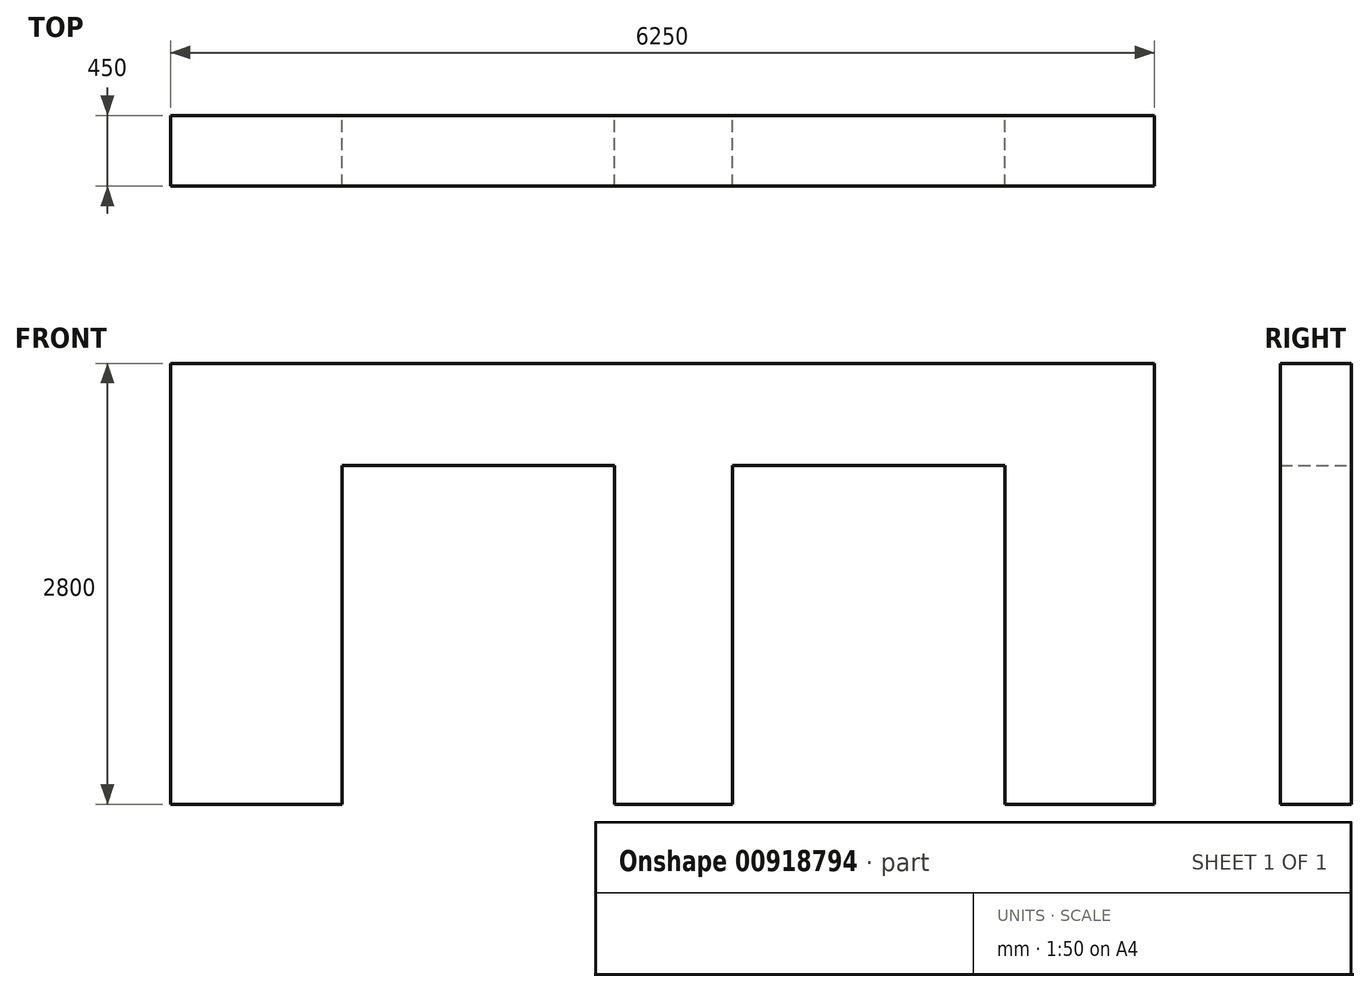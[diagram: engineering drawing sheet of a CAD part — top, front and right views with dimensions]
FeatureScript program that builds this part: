
annotation { "Feature Type Name" : "Feature", "Feature Type Description" : "" }
export const myFeature = defineFeature(function(context is Context, id is Id, definition is map)
    precondition{}
    {
        {
            var Q0;
            Q0=qCreatedBy(makeId("Front.planeOp"),FACE);
            var sketch = newSketch(context, id + "F0", { "sketchPlane" : qUnion([Q0])});
            skLineSegment(sketch, "E0.bottom", {"start": v(0, 0) * mm, "end": v(6250, 0) * mm});
            skLineSegment(sketch, "E0.top", {"start": v(0, 2800) * mm, "end": v(6250, 2800) * mm});
            skLineSegment(sketch, "E0.left", {"start": v(0, 0) * mm, "end": v(0, 2800) * mm});
            skLineSegment(sketch, "E0.right", {"start": v(6250, 0) * mm, "end": v(6250, 2800) * mm});
            skLineSegment(sketch, "E1", {"start": v(5300, 0) * mm, "end": v(5300, 2150) * mm});
            skLineSegment(sketch, "E2", {"start": v(5300, 2150) * mm, "end": v(3570, 2150) * mm});
            skLineSegment(sketch, "E3", {"start": v(3570, 2150) * mm, "end": v(3570, 0) * mm});
            skLineSegment(sketch, "E4", {"start": v(2820, 0) * mm, "end": v(2820, 2150) * mm});
            skLineSegment(sketch, "E5", {"start": v(2820, 2150) * mm, "end": v(1090, 2150) * mm});
            skLineSegment(sketch, "E6", {"start": v(1090, 2150) * mm, "end": v(1090, 0) * mm});
            skLineSegment(sketch, "E7", {"start": v(450, 2800) * mm, "end": v(450, 0) * mm, "construction": true});
            skSolve(sketch);
        }
        {
            var Q0;
            Q0=makeQuery(id+"F0.imprint","IMPRINT",FACE,{"disambiguationData":[TD([[makeQuery(id+"F0.imprint","IMPRINT",EDGE,{"derivedFrom":sQuery(id+"F0.wireOp",EDGE,"E0.top")}),-1.0]])]});
            extrude(context, id + "F1", {"entities" : qUnion([Q0]), "depth" : 450 * mm, "offsetDistance" : 25 * mm});
        }
    });
